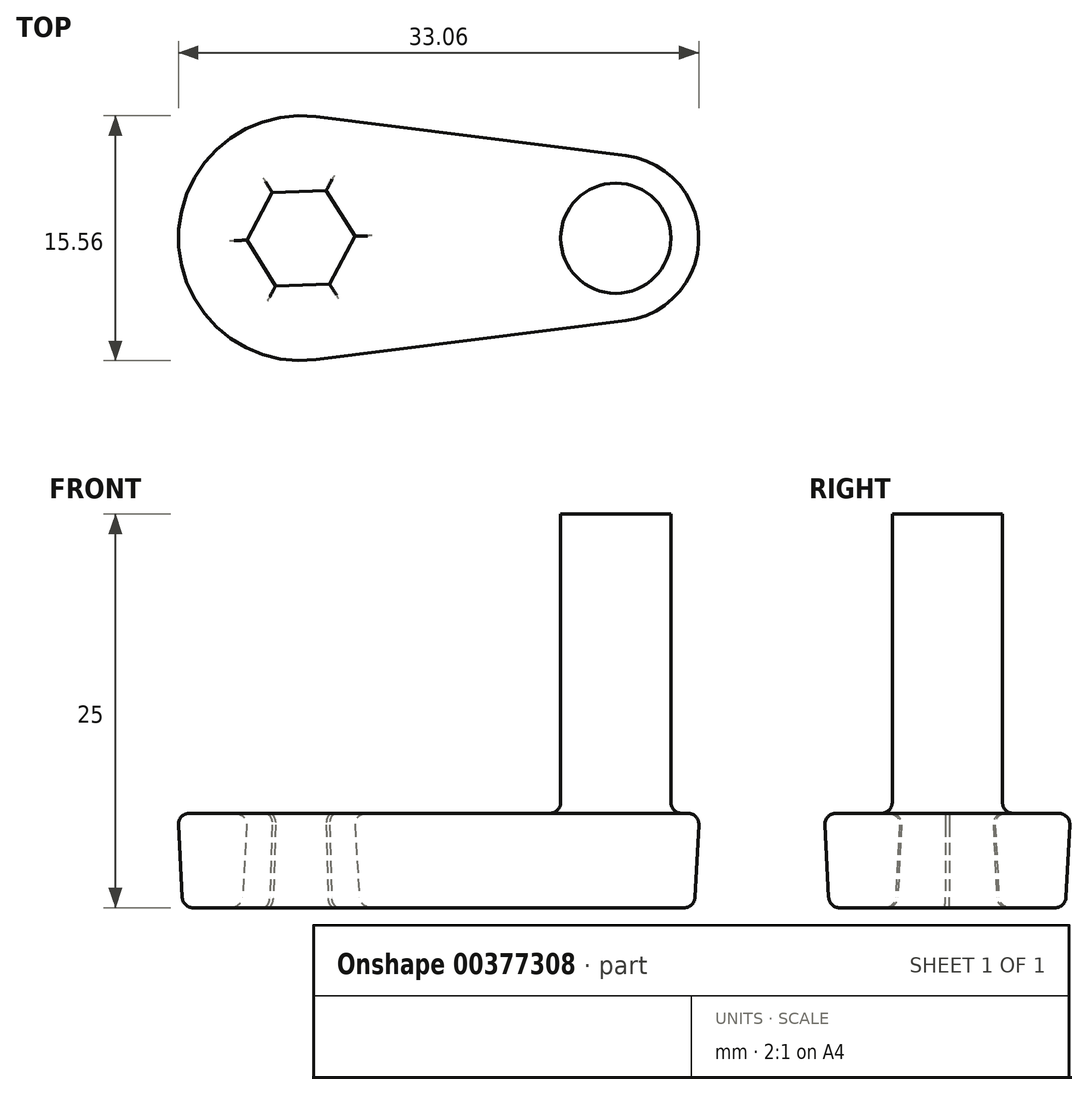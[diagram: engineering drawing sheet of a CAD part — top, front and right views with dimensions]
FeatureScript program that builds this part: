
annotation { "Feature Type Name" : "Feature", "Feature Type Description" : "" }
export const myFeature = defineFeature(function(context is Context, id is Id, definition is map)
    precondition{}
    {
        {
            var Q0;
            Q0=qCreatedBy(makeId("Top.planeOp"),FACE);
            var sketch = newSketch(context, id + "F0", { "sketchPlane" : qUnion([Q0])});
            skArc(sketch, "E0", {"start": v(-36.9, 7.44) * mm, "mid": v(-45.34, 0) * mm, "end": v(-36.9, -7.44) * mm});
            skArc(sketch, "E1", {"start": v(-17.21, -4.96) * mm, "mid": v(-12.84, 0) * mm, "end": v(-17.21, 4.96) * mm});
            skLineSegment(sketch, "E2", {"start": v(-36.9, 7.44) * mm, "end": v(-17.21, 4.96) * mm});
            skLineSegment(sketch, "E3", {"start": v(-36.9, -7.44) * mm, "end": v(-17.21, -4.96) * mm});
            skCircle(sketch, "E4", {"center": v(-17.84, 0) * mm, "radius": 3.5 * mm});
            skCircle(sketch, "E5.cCircle", {"center": v(-37.84, 0) * mm, "radius": 3.25 * mm, "construction": true});
            skLineSegment(sketch, "E5.0", {"start": v(-34.09, 0.13) * mm, "end": v(-35.85, -3.18) * mm});
            skLineSegment(sketch, "E5.1", {"start": v(-35.85, -3.18) * mm, "end": v(-39.6, -3.31) * mm});
            skLineSegment(sketch, "E5.2", {"start": v(-39.6, -3.31) * mm, "end": v(-41.6, -0.13) * mm});
            skLineSegment(sketch, "E5.3", {"start": v(-41.6, -0.13) * mm, "end": v(-39.83, 3.18) * mm});
            skLineSegment(sketch, "E5.4", {"start": v(-39.83, 3.18) * mm, "end": v(-36.08, 3.31) * mm});
            skLineSegment(sketch, "E5.5", {"start": v(-36.08, 3.31) * mm, "end": v(-34.09, 0.13) * mm});
            skPoint(sketch, "E5.0.midPoint", {"position": v(-34.97, -1.52) * mm});
            skSolve(sketch);
        }
        {
            var Q0;
            Q0=makeQuery(id+"F0.imprint","IMPRINT",FACE,{"disambiguationData":[TD([[makeQuery(id+"F0.imprint","IMPRINT",EDGE,{"derivedFrom":sQuery(id+"F0.wireOp",EDGE,"E0")}),1.0]])]});
            extrude(context, id + "F1", {"entities" : qUnion([Q0]), "depth" : 6 * mm, "hasDraft" : true, "draftAngle" : 3 * degree});
        }
        {
            var Q0;
            Q0=makeQuery(id+"F0.imprint","IMPRINT",FACE,{"disambiguationData":[TD([[makeQuery(id+"F0.imprint","IMPRINT",EDGE,{"derivedFrom":sQuery(id+"F0.wireOp",EDGE,"E4")}),1.0]])]});
            extrude(context, id + "F2", {"entities" : qUnion([Q0]), "operationType" : NewBodyOperationType.ADD, "depth" : 25 * mm});
        }
        {
            var Q0;
            {var subQ0=sQuery(id+"F0.wireOp",EDGE,"E4");Q0=makeQuery(id+"F2.boolean.opBoolean","MERGE",FACE,{"derivedFrom":[makeQuery(id+"F1.opExtrude","CAP_FACE",FACE,{"disambiguationData":[OSD([sQuery(id+"F0.wireOp",EDGE,"E0"),sQuery(id+"F0.wireOp",EDGE,"E1"),sQuery(id+"F0.wireOp",EDGE,"E2"),sQuery(id+"F0.wireOp",EDGE,"E3"),subQ0,sQuery(id+"F0.wireOp",EDGE,"E5.0"),sQuery(id+"F0.wireOp",EDGE,"E5.1"),sQuery(id+"F0.wireOp",EDGE,"E5.2"),sQuery(id+"F0.wireOp",EDGE,"E5.3"),sQuery(id+"F0.wireOp",EDGE,"E5.4"),sQuery(id+"F0.wireOp",EDGE,"E5.5")])],"isStart":true}),makeQuery(id+"F2.opExtrude","CAP_FACE",FACE,{"disambiguationData":[OSD([subQ0])],"isStart":true})]});}
            var Q1;
            Q1=makeQuery(id+"F1.opExtrude","CAP_EDGE",EDGE,{"disambiguationData":[OSD([sQuery(id+"F0.wireOp",EDGE,"E2")])],"isStart":false});
            var Q2;
            Q2=makeQuery(id+"F1.opExtrude","CAP_EDGE",EDGE,{"disambiguationData":[OSD([sQuery(id+"F0.wireOp",EDGE,"E0")])],"isStart":false});
            var Q3;
            Q3=makeQuery(id+"F1.opExtrude","CAP_EDGE",EDGE,{"disambiguationData":[OSD([sQuery(id+"F0.wireOp",EDGE,"E3")])],"isStart":false});
            var Q4;
            Q4=makeQuery(id+"F1.opExtrude","CAP_EDGE",EDGE,{"disambiguationData":[OSD([sQuery(id+"F0.wireOp",EDGE,"E1")])],"isStart":false});
            var Q5;
            Q5=makeQuery(id+"F1.opExtrude","CAP_EDGE",EDGE,{"disambiguationData":[OSD([sQuery(id+"F0.wireOp",EDGE,"E4")])],"isStart":false});
            var Q6;
            Q6=makeQuery(id+"F1.opExtrude","CAP_FACE",FACE,{"disambiguationData":[OSD([sQuery(id+"F0.wireOp",EDGE,"E0"),sQuery(id+"F0.wireOp",EDGE,"E1"),sQuery(id+"F0.wireOp",EDGE,"E2"),sQuery(id+"F0.wireOp",EDGE,"E3"),sQuery(id+"F0.wireOp",EDGE,"E4"),sQuery(id+"F0.wireOp",EDGE,"E5.0"),sQuery(id+"F0.wireOp",EDGE,"E5.1"),sQuery(id+"F0.wireOp",EDGE,"E5.2"),sQuery(id+"F0.wireOp",EDGE,"E5.3"),sQuery(id+"F0.wireOp",EDGE,"E5.4"),sQuery(id+"F0.wireOp",EDGE,"E5.5")])],"isStart":false});
            fillet(context, id + "F3", {"entities" : qUnion([Q0, Q1, Q2, Q3, Q4, Q5, Q6]), "radius" : .7 * mm, "tangentPropagation" : true, "allowEdgeOverflow" : false});
        }
    });
